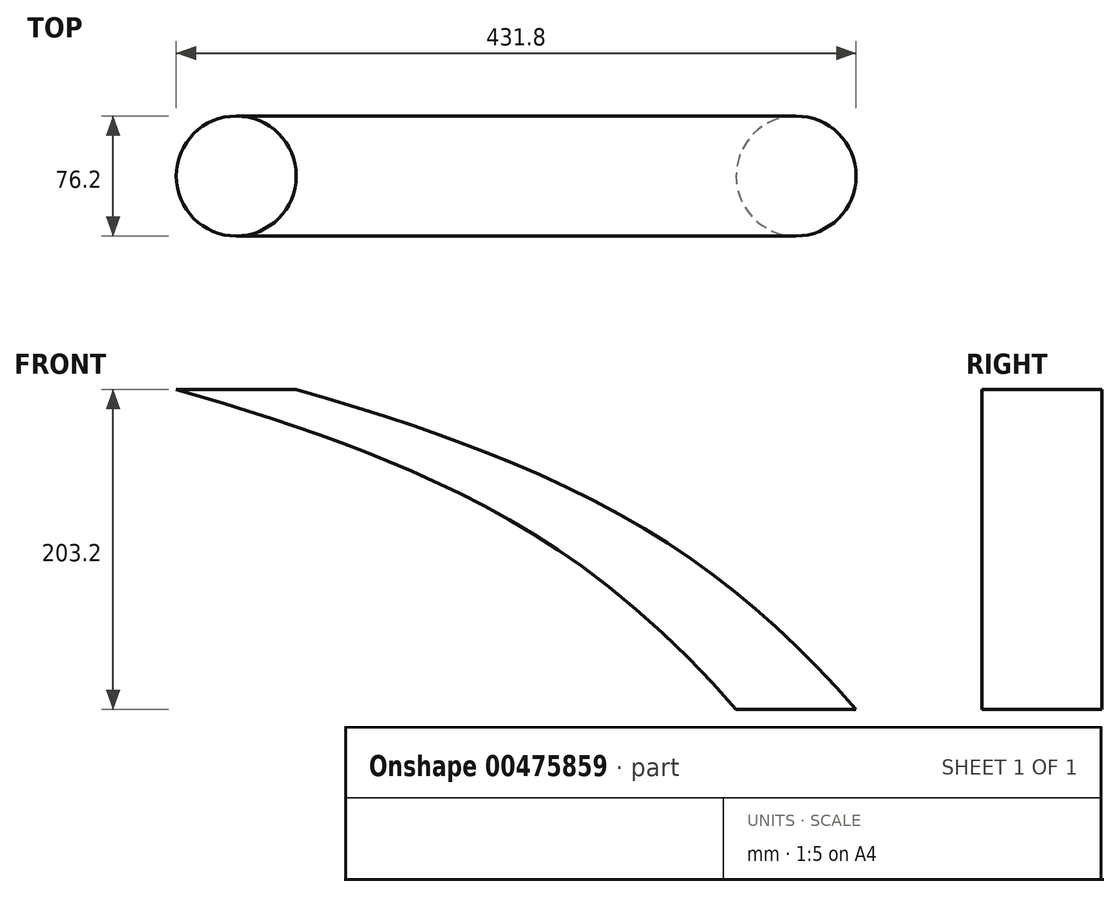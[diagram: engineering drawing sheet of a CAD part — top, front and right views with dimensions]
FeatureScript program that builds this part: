
annotation { "Feature Type Name" : "Feature", "Feature Type Description" : "" }
export const myFeature = defineFeature(function(context is Context, id is Id, definition is map)
    precondition{}
    {
        {
            var Q0;
            Q0=qCreatedBy(makeId("Front.planeOp"),FACE);
            var sketch = newSketch(context, id + "F0", { "sketchPlane" : qUnion([Q0])});
            skLineSegment(sketch, "E0", {"start": v(87.97, -54.47) * mm, "end": v(126.07, -54.47) * mm});
            skFitSpline(sketch, "E1", {"points": [v(-229.53, 148.73) * mm, v(126.07, -54.47) * mm], "startDerivative": vector(266.7, -304.8) * mm, "endDerivative": vector(266.7, -304.8) * mm});
            skPoint(sketch, "E2.endSnap0", {"position": v(-51.73, -54.47) * mm});
            skLineSegment(sketch, "E3", {"start": v(37.17, 47.13) * mm, "end": v(37.17, -54.47) * mm});
            skFitSpline(sketch, "E4", {"points": [v(-229.53, 148.73) * mm, v(126.07, -54.47) * mm], "startDerivative": vector(533.4, -152.4) * mm, "endDerivative": vector(266.7, -304.8) * mm});
            skSolve(sketch);
        }
        {
            var Q0;
            Q0=qCreatedBy(makeId("Top.planeOp"),FACE);
            var sketch = newSketch(context, id + "F1", { "sketchPlane" : qUnion([Q0])});
            skCircle(sketch, "E5", {"center": v(0, 0) * mm, "radius": 38.1 * mm});
            skSolve(sketch);
        }
        {
            var Q0;
            Q0=makeQuery(id+"F1.imprint","IMPRINT",FACE,{"disambiguationData":[TD([[makeQuery(id+"F1.imprint","IMPRINT",EDGE,{"derivedFrom":sQuery(id+"F1.wireOp",EDGE,"E5")}),1.0]])]});
            extrude(context, id + "F2", {"entities" : qUnion([Q0]), "depth" : 203.2 * mm});
        }
        {
            var Q0;
            Q0=makeQuery(id+"F2.opExtrude","CAP_FACE",FACE,{"disambiguationData":[OSD([sQuery(id+"F1.wireOp",EDGE,"E5")])],"isStart":false});
            var Q1;
            Q1=sQuery(id+"F0.wireOp",EDGE,"E4");
            sweep(context, id + "F3", {"profiles" : qUnion([Q0]), "path" : qUnion([Q1]), "keepProfileOrientation" : true});
        }
        {
            var Q0;
            Q0=makeQuery(id+"F2.opExtrude","SWEPT_BODY",BODY,{"disambiguationData":[OSD([sQuery(id+"F1.wireOp",EDGE,"E5")])]});
            deleteBodies(context, id + "F4", {"entities" : qUnion([Q0])});
        }
    });
